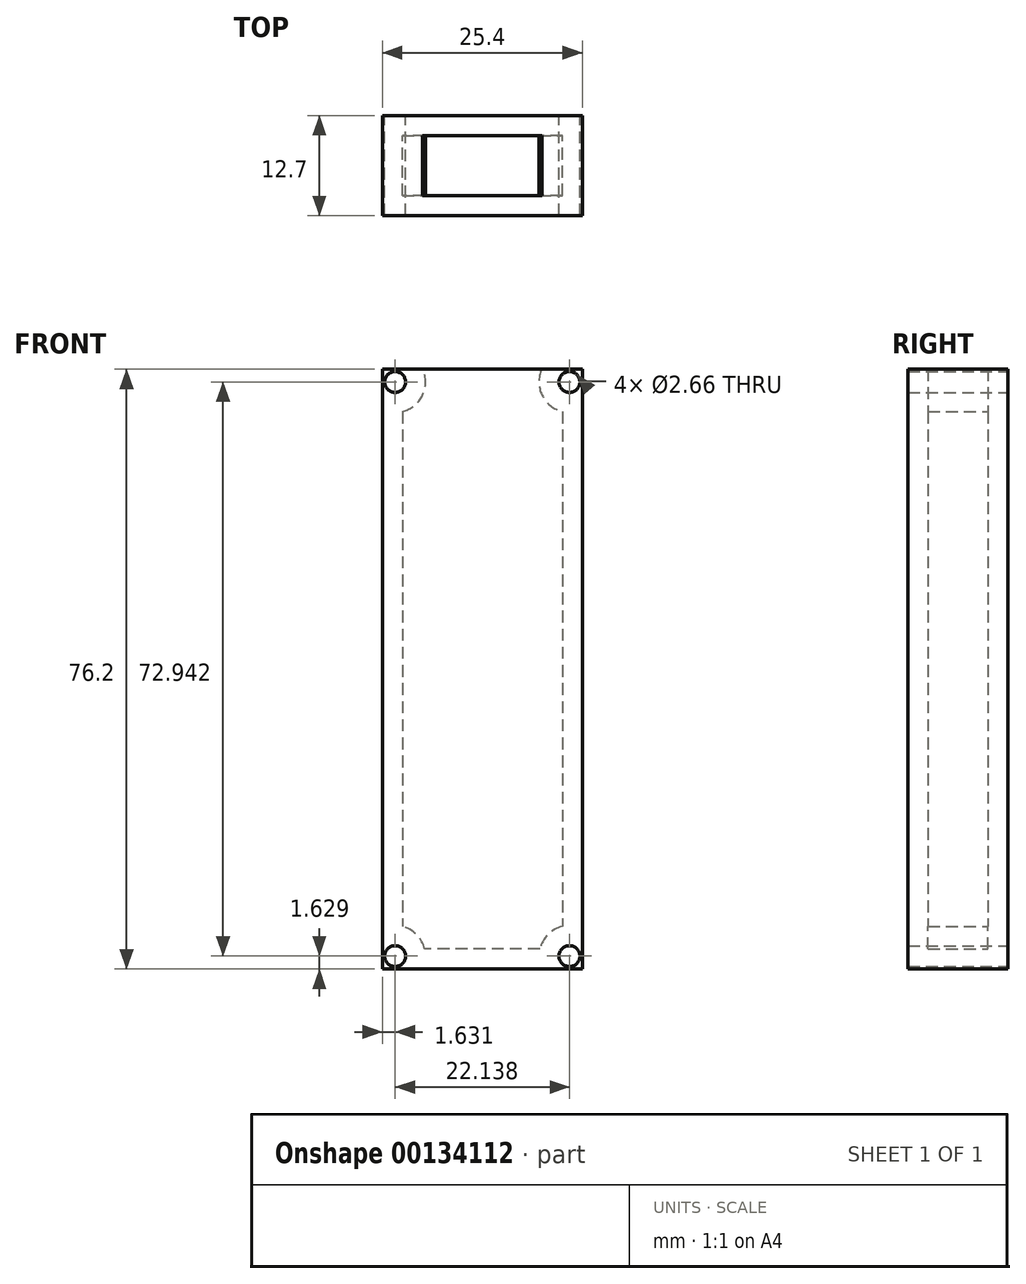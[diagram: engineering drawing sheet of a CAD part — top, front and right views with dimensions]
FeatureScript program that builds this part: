
annotation { "Feature Type Name" : "Feature", "Feature Type Description" : "" }
export const myFeature = defineFeature(function(context is Context, id is Id, definition is map)
    precondition{}
    {
        {
            var Q0;
            Q0=qCreatedBy(makeId("Front.planeOp"),FACE);
            var sketch = newSketch(context, id + "F0", { "sketchPlane" : qUnion([Q0])});
            skLineSegment(sketch, "E0.bottom", {"start": v(12.7, 38.1) * mm, "end": v(-12.7, 38.1) * mm});
            skLineSegment(sketch, "E0.top", {"start": v(12.7, -38.1) * mm, "end": v(-12.7, -38.1) * mm});
            skLineSegment(sketch, "E0.left", {"start": v(12.7, 38.1) * mm, "end": v(12.7, -38.1) * mm});
            skLineSegment(sketch, "E0.right", {"start": v(-12.7, 38.1) * mm, "end": v(-12.7, -38.1) * mm});
            skPoint(sketch, "E0.middle", {"position": v(0, 0) * mm});
            skCircle(sketch, "E1", {"center": v(-11.07, 36.47) * mm, "radius": 1.33 * mm});
            skCircle(sketch, "E2.MirrorC", {"center": v(11.07, 36.47) * mm, "radius": 1.33 * mm});
            skCircle(sketch, "E3.MirrorC", {"center": v(-11.07, -36.47) * mm, "radius": 1.33 * mm});
            skCircle(sketch, "E4.MirrorC", {"center": v(11.07, -36.47) * mm, "radius": 1.33 * mm});
            skSolve(sketch);
        }
        {
            var Q0;
            Q0=makeQuery(id+"F0.imprint","IMPRINT",FACE,{"disambiguationData":[TD([[makeQuery(id+"F0.imprint","IMPRINT",EDGE,{"derivedFrom":sQuery(id+"F0.wireOp",EDGE,"E0.bottom")}),1.0]])]});
            extrude(context, id + "F1", {"entities" : qUnion([Q0]), "depth" : 12.7 * mm});
        }
        {
            var Q0;
            Q0=makeQuery(id+"F1.opExtrude","SWEPT_FACE",FACE,{"disambiguationData":[OSD([sQuery(id+"F0.wireOp",EDGE,"E0.bottom")])]});
            shell(context, id + "F2", {"entities" : qUnion([Q0]), "thickness" : 2.54 * mm});
        }
    });
